# Revit family: Haworth_Very_Chair_Task_Executive_AP_PRELIMINARY
name_source: partatom
category: Furniture
revit_build: Autodesk Revit 2018 (Build: 20170223_1515(x64)
units: mm (PartAtom-declared; Revit-internal decimal feet)

## family parameters
Always vertical = Yes
Cut with Voids When Loaded = No
OmniClass Number = 23.40.70.14.64.11
OmniClass Title = Office Furniture
Room Calculation Point = No
Shared = No
Work Plane-Based = No

## types (4) — shared parameters
Arm Cap Finish = Haworth _ Paint _ Smoke
Assembly Code = E2020200
Base Finish = Haworth _ Metal _ Polished Aluminum
Caster Finish = Haworth _ Polymer _ Black
Depth = 737 mm
Description = Haworth - Very - Chair - Executive - Task
Headrest = Yes
Headrest Backer = Haworth _ Fabric _ Zinger _ Gravel NI-4
Lumbar = Yes
Manufacturer = Haworth
Model = SEVYEXX
Revision Number = 3
Shell Finish = Haworth _ Metal _ Polished Aluminum
Size = Verify Final Dim. w/Haworth
Sustainability Info = https://www.haworth.com
URL = https://www.haworth.com
URL - Product = https://www.haworth.com
Warranty = http://www.haworth.com
Width = 737 mm

## per-type parameters (varying)
| type | 4D Arms | Adjustable Arms | Armless | Arms |
| Height Adjustable Arms | Yes | Yes | No | Yes |
| Fixed Arms | No | No | No | Yes |
| 4D Arms | Yes | Yes | No | Yes |
| Without Arms | No | No | Yes | No |

type visibility flags (boolean, named after types; folded from table):
- Height Adjustable Arms: Yes: (none)
- Fixed Arms: Yes: Fixed Arms
- 4D Arms: Yes: (none)
- Without Arms: Yes: (none)

## geometry (parser evidence)
native form markers: Sweep x16
no freeform markers — native parametric forms only
